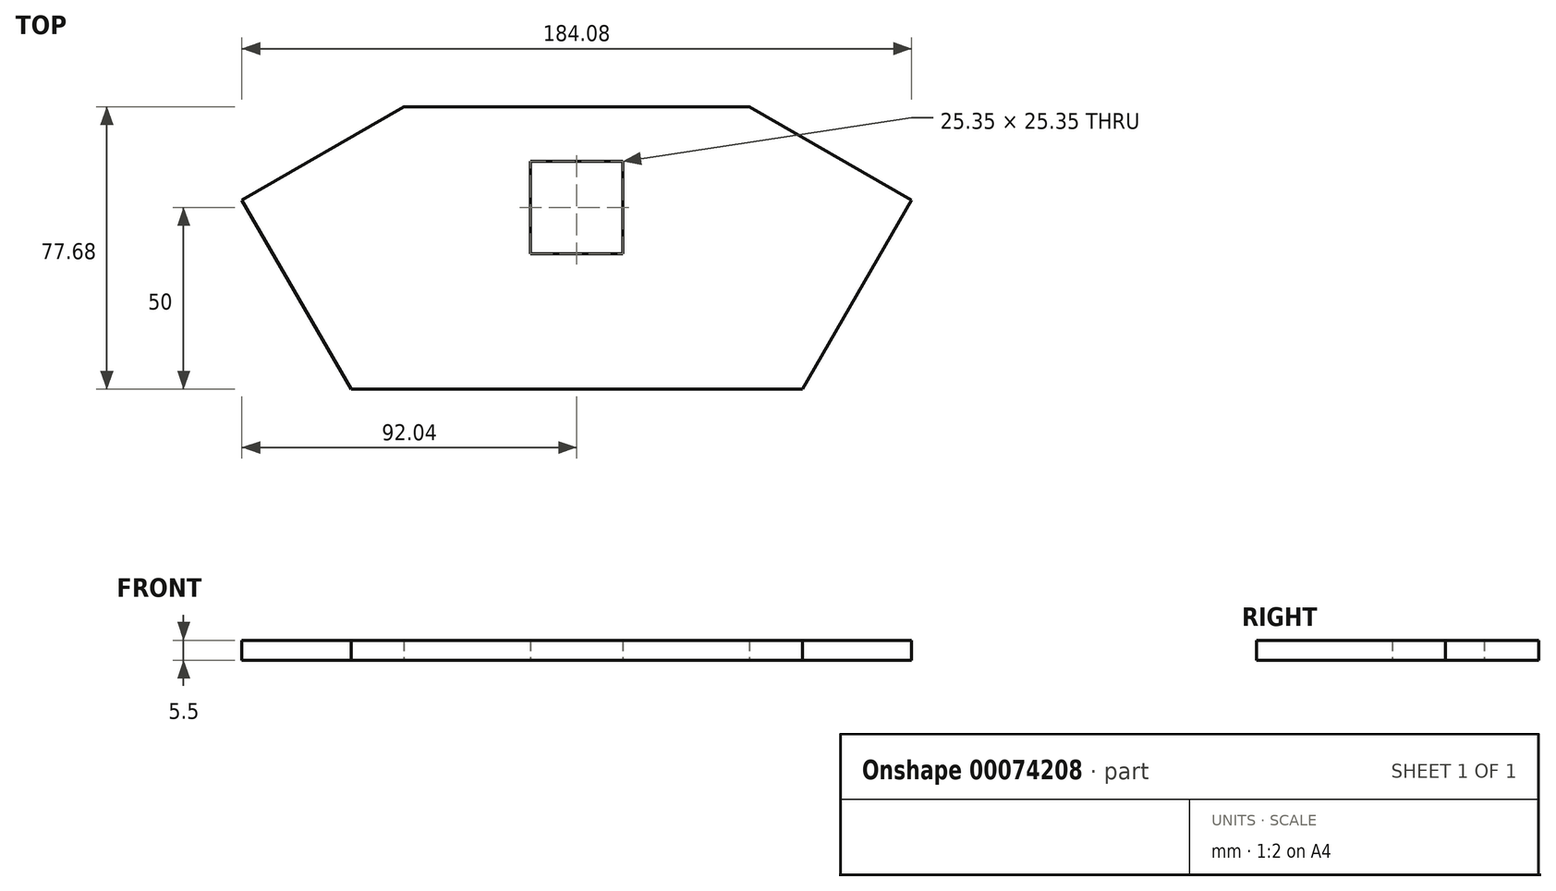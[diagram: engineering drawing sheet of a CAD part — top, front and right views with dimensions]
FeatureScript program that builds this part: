
annotation { "Feature Type Name" : "Feature", "Feature Type Description" : "" }
export const myFeature = defineFeature(function(context is Context, id is Id, definition is map)
    precondition{}
    {
        {
            var Q0;
            Q0=qCreatedBy(makeId("Top.planeOp"),FACE);
            var sketch = newSketch(context, id + "F0", { "sketchPlane" : qUnion([Q0])});
            skLineSegment(sketch, "E0.rect.bottom", {"start": v(12.67, 12.68) * mm, "end": v(-12.68, 12.68) * mm});
            skLineSegment(sketch, "E0.rect.top", {"start": v(12.68, -12.68) * mm, "end": v(-12.67, -12.68) * mm});
            skLineSegment(sketch, "E0.rect.left", {"start": v(12.67, 12.68) * mm, "end": v(12.68, -12.68) * mm});
            skLineSegment(sketch, "E0.rect.right", {"start": v(-12.68, 12.68) * mm, "end": v(-12.67, -12.68) * mm});
            skPoint(sketch, "E0.rect.middle", {"position": v(0, 0) * mm});
            skLineSegment(sketch, "E1", {"start": v(0, 12.68) * mm, "end": v(0, -12.68) * mm, "construction": true});
            skLineSegment(sketch, "E2", {"start": v(-47.5, 27.67) * mm, "end": v(47.5, 27.67) * mm});
            skLineSegment(sketch, "E3", {"start": v(-44.72, -40) * mm, "end": v(44.72, -40) * mm, "construction": true});
            skLineSegment(sketch, "E4", {"start": v(44.72, -40) * mm, "end": v(74.72, 11.96) * mm, "construction": true});
            skLineSegment(sketch, "E5", {"start": v(74.72, 11.96) * mm, "end": v(47.5, 27.68) * mm});
            skLineSegment(sketch, "E6", {"start": v(44.72, -40) * mm, "end": v(44.72, 74) * mm, "construction": true});
            skLineSegment(sketch, "E7", {"start": v(44.72, -40) * mm, "end": v(62.04, -50) * mm, "construction": true});
            skLineSegment(sketch, "E8", {"start": v(62.04, -50) * mm, "end": v(92.04, 1.96) * mm});
            skLineSegment(sketch, "E9", {"start": v(92.04, 1.96) * mm, "end": v(74.72, 11.96) * mm});
            skLineSegment(sketch, "E10", {"start": v(62.04, -50) * mm, "end": v(-62.04, -50) * mm});
            skLineSegment(sketch, "E11.MirrorCS", {"start": v(-62.04, -50) * mm, "end": v(-92.04, 1.96) * mm});
            skLineSegment(sketch, "E12", {"start": v(-92.04, 1.96) * mm, "end": v(-47.5, 27.67) * mm});
            skSolve(sketch);
        }
        {
            var Q0;
            Q0 = qSketchRegion(id + "F0", true);
            extrude(context, id + "F1", {"entities" : qUnion([Q0]), "depth" : 5.5 * mm});
        }
    });
